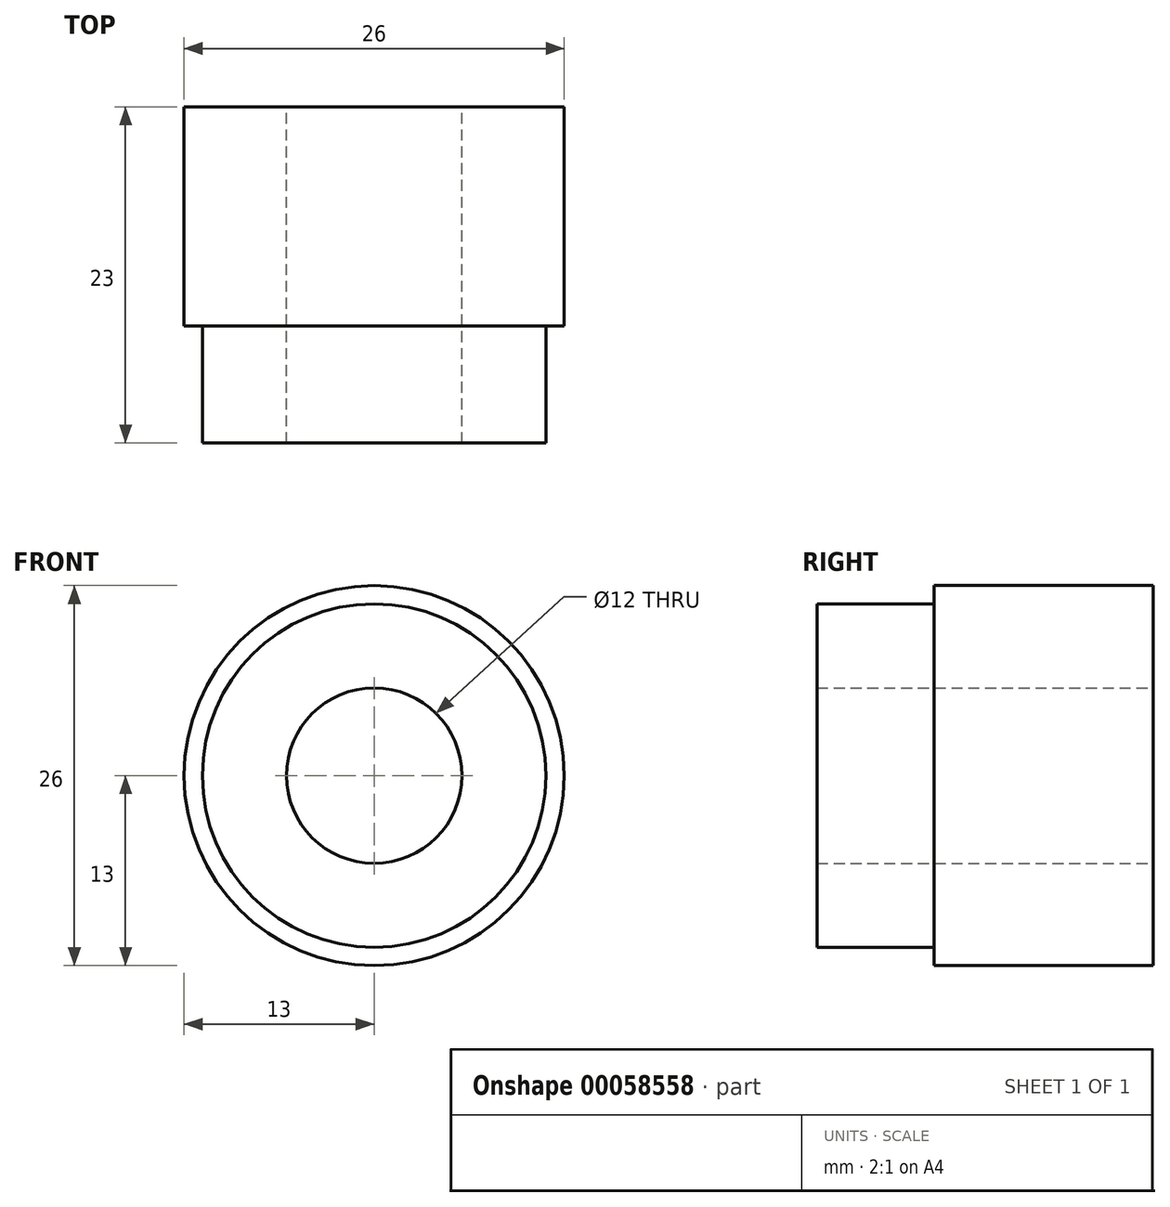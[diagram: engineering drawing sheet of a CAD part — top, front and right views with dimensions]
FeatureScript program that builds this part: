
annotation { "Feature Type Name" : "Feature", "Feature Type Description" : "" }
export const myFeature = defineFeature(function(context is Context, id is Id, definition is map)
    precondition{}
    {
        {
            var Q0;
            Q0=qCreatedBy(makeId("Front.planeOp"),FACE);
            var sketch = newSketch(context, id + "F0", { "sketchPlane" : qUnion([Q0])});
            skCircle(sketch, "E0", {"center": v(0, 0) * mm, "radius": 11.75 * mm});
            skSolve(sketch);
        }
        {
            var Q0;
            Q0 = qSketchRegion(id + "F0", true);
            extrude(context, id + "F1", {"entities" : qUnion([Q0]), "depth" : 8 * mm});
        }
        {
            var Q0;
            Q0=makeQuery(id+"F1.opExtrude","CAP_FACE",FACE,{"disambiguationData":[OSD([sQuery(id+"F0.wireOp",EDGE,"E0")])],"isStart":true});
            var sketch = newSketch(context, id + "F2", { "sketchPlane" : qUnion([Q0])});
            skCircle(sketch, "E1", {"center": v(0, 0) * mm, "radius": 13 * mm});
            skSolve(sketch);
        }
        {
            var Q0;
            Q0 = qSketchRegion(id + "F2", true);
            extrude(context, id + "F3", {"entities" : qUnion([Q0]), "operationType" : NewBodyOperationType.ADD, "depth" : 15 * mm});
        }
        {
            var Q0;
            Q0=makeQuery(id+"F3.opExtrude","CAP_FACE",FACE,{"disambiguationData":[OSD([sQuery(id+"F2.wireOp",EDGE,"E1")])],"isStart":false});
            var sketch = newSketch(context, id + "F4", { "sketchPlane" : qUnion([Q0])});
            skCircle(sketch, "E2", {"center": v(0, 0) * mm, "radius": 6 * mm});
            skSolve(sketch);
        }
        {
            var Q0;
            Q0 = qSketchRegion(id + "F4", true);
            extrude(context, id + "F5", {"entities" : qUnion([Q0]), "operationType" : NewBodyOperationType.REMOVE, "oppositeDirection" : true, "depth" : 25 * mm});
        }
    });
